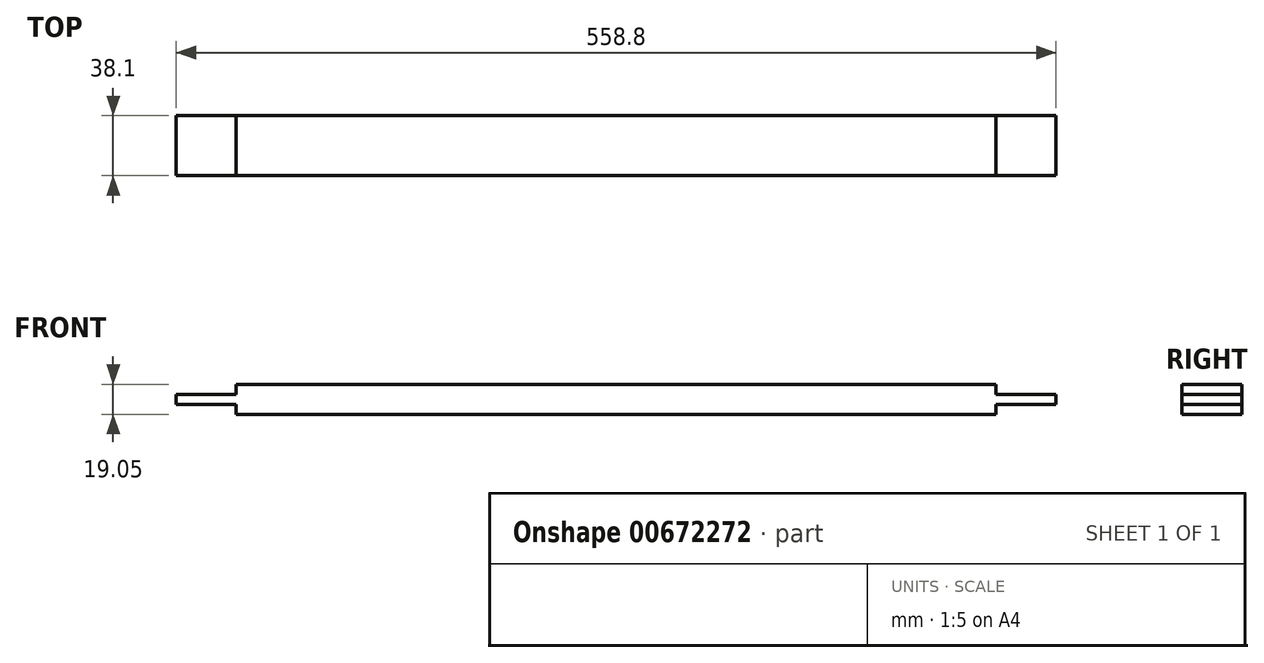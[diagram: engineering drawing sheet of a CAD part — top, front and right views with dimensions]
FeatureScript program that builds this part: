
annotation { "Feature Type Name" : "Feature", "Feature Type Description" : "" }
export const myFeature = defineFeature(function(context is Context, id is Id, definition is map)
    precondition{}
    {
        {
            var Q0;
            Q0=qCreatedBy(makeId("Front.planeOp"),FACE);
            var sketch = newSketch(context, id + "F0", { "sketchPlane" : qUnion([Q0])});
            skLineSegment(sketch, "E0.bottom", {"start": v(38.1, -6.35) * mm, "end": v(520.7, -6.35) * mm});
            skLineSegment(sketch, "E0.top", {"start": v(38.1, 12.7) * mm, "end": v(520.7, 12.7) * mm});
            skLineSegment(sketch, "E0.left", {"start": v(0, 0) * mm, "end": v(0, 6.35) * mm});
            skLineSegment(sketch, "E0.right", {"start": v(558.8, 0) * mm, "end": v(558.8, 6.35) * mm});
            skLineSegment(sketch, "E1.top", {"start": v(0, 0) * mm, "end": v(38.1, 0) * mm});
            skLineSegment(sketch, "E1.right", {"start": v(38.1, -6.35) * mm, "end": v(38.1, 0) * mm});
            skLineSegment(sketch, "E2.top", {"start": v(0, 6.35) * mm, "end": v(38.1, 6.35) * mm});
            skLineSegment(sketch, "E2.right", {"start": v(38.1, 12.7) * mm, "end": v(38.1, 6.35) * mm});
            skLineSegment(sketch, "E3.top", {"start": v(558.8, 0) * mm, "end": v(520.7, 0) * mm});
            skLineSegment(sketch, "E3.right", {"start": v(520.7, -6.35) * mm, "end": v(520.7, 0) * mm});
            skLineSegment(sketch, "E4.top", {"start": v(558.8, 6.35) * mm, "end": v(520.7, 6.35) * mm});
            skLineSegment(sketch, "E4.right", {"start": v(520.7, 12.7) * mm, "end": v(520.7, 6.35) * mm});
            skSolve(sketch);
        }
        {
            var Q0;
            Q0=makeQuery(id+"F0.imprint","IMPRINT",FACE,{"disambiguationData":[TD([[makeQuery(id+"F0.imprint","IMPRINT",EDGE,{"derivedFrom":sQuery(id+"F0.wireOp",EDGE,"E0.bottom")}),1.0]])]});
            extrude(context, id + "F1", {"entities" : qUnion([Q0]), "depth" : 38.1 * mm, "offsetDistance" : 25.4 * mm});
        }
    });
